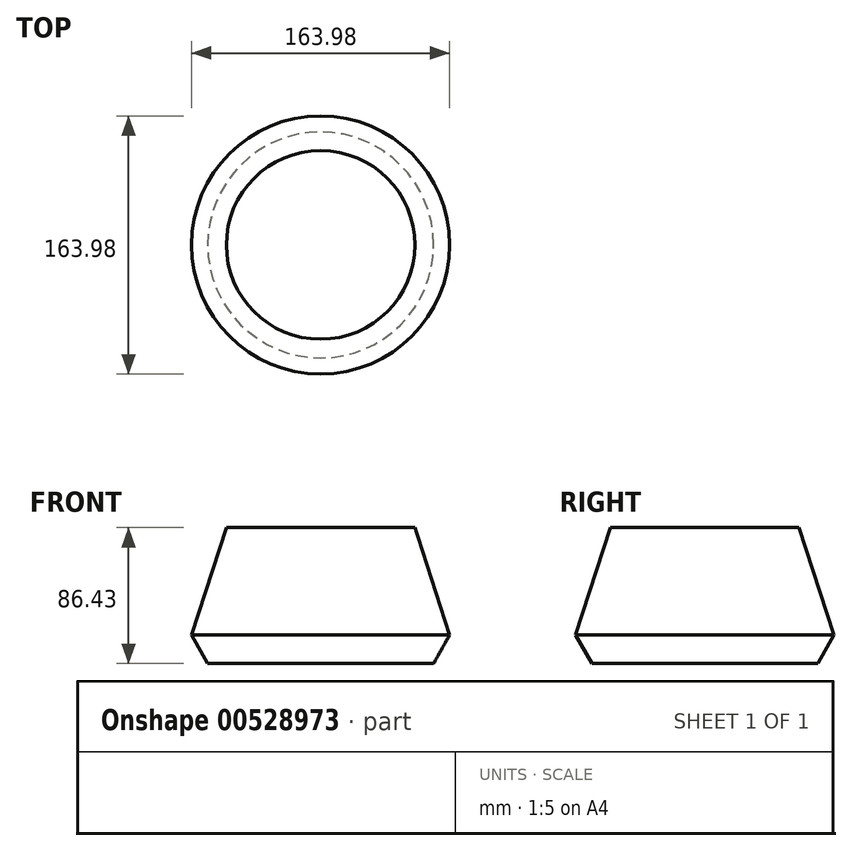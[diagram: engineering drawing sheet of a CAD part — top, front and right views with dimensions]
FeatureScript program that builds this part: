
annotation { "Feature Type Name" : "Feature", "Feature Type Description" : "" }
export const myFeature = defineFeature(function(context is Context, id is Id, definition is map)
    precondition{}
    {
        {
            var Q0;
            Q0=qCreatedBy(makeId("Front.planeOp"),FACE);
            var sketch = newSketch(context, id + "F0", { "sketchPlane" : qUnion([Q0])});
            skLineSegment(sketch, "E0", {"start": v(0, 123.6) * mm, "end": v(0, -98.88) * mm});
            skLineSegment(sketch, "E1", {"start": v(0, 86.43) * mm, "end": v(59.87, 86.43) * mm});
            skLineSegment(sketch, "E2", {"start": v(59.87, 86.43) * mm, "end": v(81.99, 18.26) * mm});
            skLineSegment(sketch, "E3", {"start": v(81.99, 18.26) * mm, "end": v(71.75, 0) * mm});
            skLineSegment(sketch, "E4", {"start": v(71.75, 0) * mm, "end": v(0, 0) * mm});
            skSolve(sketch);
        }
        {
            var Q0;
            Q0 = qSketchRegion(id + "F0", true);
            var Q1;
            Q1=sQuery(id+"F0.wireOp",EDGE,"E0");
            revolve(context, id + "F1", {"entities" : qUnion([Q0]), "axis" : qUnion([Q1]), "revolveType" : RevolveType.FULL});
        }
    });
